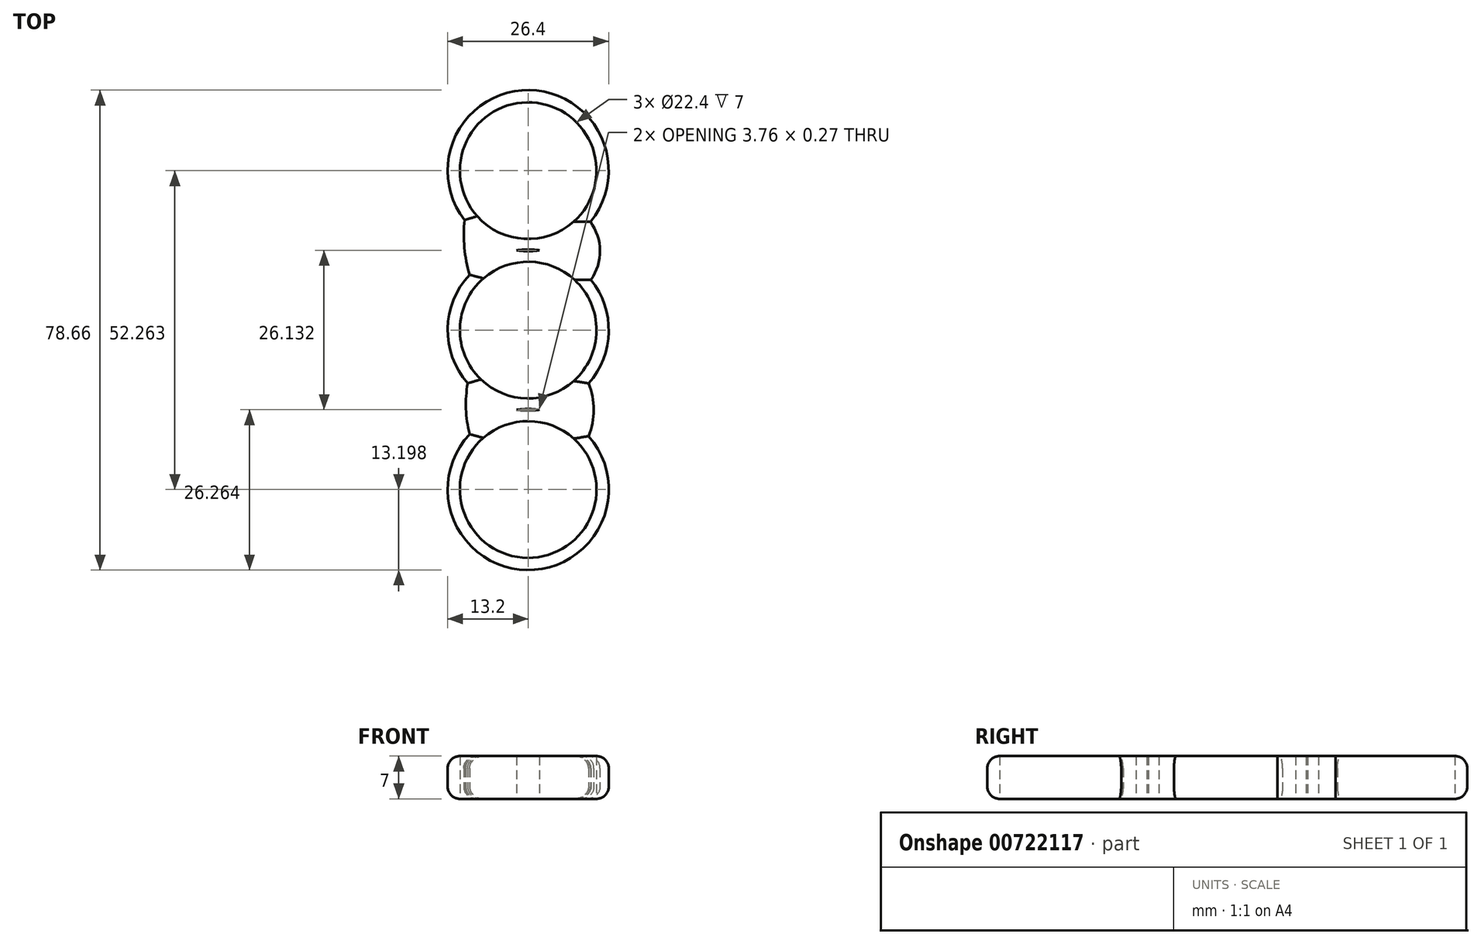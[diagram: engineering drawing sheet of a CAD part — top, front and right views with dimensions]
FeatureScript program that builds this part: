
annotation { "Feature Type Name" : "Feature", "Feature Type Description" : "" }
export const myFeature = defineFeature(function(context is Context, id is Id, definition is map)
    precondition{}
    {
        {
            var Q0;
            Q0=qCreatedBy(makeId("Top.planeOp"),FACE);
            var sketch = newSketch(context, id + "F0", { "sketchPlane" : qUnion([Q0])});
            skCircle(sketch, "E0", {"center": v(0, 0) * mm, "radius": 11.2 * mm});
            skCircle(sketch, "E1", {"center": v(0, 0) * mm, "radius": 13.2 * mm});
            skCircle(sketch, "E2", {"center": v(0, 26.13) * mm, "radius": 11.2 * mm});
            skCircle(sketch, "E3", {"center": v(0, 26.13) * mm, "radius": 13.2 * mm});
            skCircle(sketch, "E4.1.0", {"center": v(0, -26.13) * mm, "radius": 13.2 * mm});
            skCircle(sketch, "E4.1.1", {"center": v(0, -26.13) * mm, "radius": 11.2 * mm});
            skArc(sketch, "E5", {"start": v(10.3, 8.25) * mm, "mid": v(11.77, 13.02) * mm, "end": v(10.2, 17.75) * mm});
            skArc(sketch, "E6", {"start": v(-10.43, 18.04) * mm, "mid": v(-10.45, 13.51) * mm, "end": v(-9.6, 9.06) * mm});
            skArc(sketch, "E7", {"start": v(-9.91, -8.71) * mm, "mid": v(-10.17, -13.38) * mm, "end": v(-9.35, -17.97) * mm});
            skArc(sketch, "E8", {"start": v(9.9, -17.4) * mm, "mid": v(10.76, -13.07) * mm, "end": v(9.9, -8.74) * mm});
            skSolve(sketch);
        }
        {
            var Q0;
            Q0 = qSketchRegion(id + "F0", true);
            extrude(context, id + "F1", {"entities" : qUnion([Q0]), "depth" : 7 * mm, "offsetDistance" : 25 * mm});
        }
        {
            var Q0;
            {var subQ0=sQuery(id+"F0.wireOp",EDGE,"E3");Q0=makeQuery(id+"F1.opExtrude","CAP_EDGE",EDGE,{"disambiguationData":[OSD([subQ0]),TDD([makeQuery(id+"F0.imprint","IMPRINT",EDGE,{"disambiguationData":[TD([[makeQuery(id+"F0.imprint","INTERSECT",VERTEX,{"derivedFrom":[subQ0,sQuery(id+"F0.wireOp",EDGE,"E5")]}),-1.0]])],"derivedFrom":subQ0})])],"isStart":false});}
            var Q1;
            Q1=makeQuery(id+"F1.opExtrude","CAP_EDGE",EDGE,{"disambiguationData":[OSD([sQuery(id+"F0.wireOp",EDGE,"E5")])],"isStart":false});
            var Q2;
            {var subQ0=sQuery(id+"F0.wireOp",EDGE,"E1");Q2=makeQuery(id+"F1.opExtrude","CAP_EDGE",EDGE,{"disambiguationData":[OSD([subQ0]),TDD([makeQuery(id+"F0.imprint","IMPRINT",EDGE,{"disambiguationData":[TD([[makeQuery(id+"F0.imprint","INTERSECT",VERTEX,{"derivedFrom":[subQ0,sQuery(id+"F0.wireOp",EDGE,"E5")]}),1.0]])],"derivedFrom":subQ0})])],"isStart":false});}
            var Q3;
            Q3=makeQuery(id+"F1.opExtrude","CAP_EDGE",EDGE,{"disambiguationData":[OSD([sQuery(id+"F0.wireOp",EDGE,"E8")])],"isStart":false});
            var Q4;
            {var subQ0=sQuery(id+"F0.wireOp",EDGE,"E4.1.0");Q4=makeQuery(id+"F1.opExtrude","CAP_EDGE",EDGE,{"disambiguationData":[OSD([subQ0]),TDD([makeQuery(id+"F0.imprint","IMPRINT",EDGE,{"disambiguationData":[TD([[makeQuery(id+"F0.imprint","INTERSECT",VERTEX,{"derivedFrom":[subQ0,sQuery(id+"F0.wireOp",EDGE,"E8")]}),1.0]])],"derivedFrom":subQ0})])],"isStart":false});}
            var Q5;
            Q5=makeQuery(id+"F1.opExtrude","CAP_EDGE",EDGE,{"disambiguationData":[OSD([sQuery(id+"F0.wireOp",EDGE,"E7")])],"isStart":false});
            var Q6;
            {var subQ0=sQuery(id+"F0.wireOp",EDGE,"E1");Q6=makeQuery(id+"F1.opExtrude","CAP_EDGE",EDGE,{"disambiguationData":[OSD([subQ0]),TDD([makeQuery(id+"F0.imprint","IMPRINT",EDGE,{"disambiguationData":[TD([[makeQuery(id+"F0.imprint","INTERSECT",VERTEX,{"derivedFrom":[subQ0,sQuery(id+"F0.wireOp",EDGE,"E6")]}),-1.0]])],"derivedFrom":subQ0})])],"isStart":false});}
            var Q7;
            Q7=makeQuery(id+"F1.opExtrude","CAP_EDGE",EDGE,{"disambiguationData":[OSD([sQuery(id+"F0.wireOp",EDGE,"E6")])],"isStart":false});
            fillet(context, id + "F2", {"entities" : qUnion([Q0, Q1, Q2, Q3, Q4, Q5, Q6, Q7]), "radius" : 2 * mm, "tangentPropagation" : true, "allowEdgeOverflow" : false});
        }
        {
            var Q0;
            {var subQ0=sQuery(id+"F0.wireOp",EDGE,"E4.1.0");Q0=makeQuery(id+"F1.opExtrude","CAP_EDGE",EDGE,{"disambiguationData":[OSD([subQ0]),TDD([makeQuery(id+"F0.imprint","IMPRINT",EDGE,{"disambiguationData":[TD([[makeQuery(id+"F0.imprint","INTERSECT",VERTEX,{"derivedFrom":[subQ0,sQuery(id+"F0.wireOp",EDGE,"E8")]}),1.0]])],"derivedFrom":subQ0})])],"isStart":true});}
            var Q1;
            Q1=makeQuery(id+"F1.opExtrude","CAP_EDGE",EDGE,{"disambiguationData":[OSD([sQuery(id+"F0.wireOp",EDGE,"E8")])],"isStart":true});
            var Q2;
            {var subQ0=sQuery(id+"F0.wireOp",EDGE,"E1");Q2=makeQuery(id+"F1.opExtrude","CAP_EDGE",EDGE,{"disambiguationData":[OSD([subQ0]),TDD([makeQuery(id+"F0.imprint","IMPRINT",EDGE,{"disambiguationData":[TD([[makeQuery(id+"F0.imprint","INTERSECT",VERTEX,{"derivedFrom":[subQ0,sQuery(id+"F0.wireOp",EDGE,"E5")]}),1.0]])],"derivedFrom":subQ0})])],"isStart":true});}
            var Q3;
            Q3=makeQuery(id+"F1.opExtrude","CAP_EDGE",EDGE,{"disambiguationData":[OSD([sQuery(id+"F0.wireOp",EDGE,"E5")])],"isStart":true});
            var Q4;
            Q4=makeQuery(id+"F1.opExtrude","CAP_EDGE",EDGE,{"disambiguationData":[OSD([sQuery(id+"F0.wireOp",EDGE,"E6")])],"isStart":true});
            var Q5;
            Q5=makeQuery(id+"F1.opExtrude","CAP_EDGE",EDGE,{"disambiguationData":[OSD([sQuery(id+"F0.wireOp",EDGE,"E7")])],"isStart":true});
            var Q6;
            {var subQ0=sQuery(id+"F0.wireOp",EDGE,"E3");Q6=makeQuery(id+"F1.opExtrude","CAP_EDGE",EDGE,{"disambiguationData":[OSD([subQ0]),TDD([makeQuery(id+"F0.imprint","IMPRINT",EDGE,{"disambiguationData":[TD([[makeQuery(id+"F0.imprint","INTERSECT",VERTEX,{"derivedFrom":[subQ0,sQuery(id+"F0.wireOp",EDGE,"E5")]}),-1.0]])],"derivedFrom":subQ0})])],"isStart":true});}
            var Q7;
            {var subQ0=sQuery(id+"F0.wireOp",EDGE,"E1");Q7=makeQuery(id+"F1.opExtrude","CAP_EDGE",EDGE,{"disambiguationData":[OSD([subQ0]),TDD([makeQuery(id+"F0.imprint","IMPRINT",EDGE,{"disambiguationData":[TD([[makeQuery(id+"F0.imprint","INTERSECT",VERTEX,{"derivedFrom":[subQ0,sQuery(id+"F0.wireOp",EDGE,"E6")]}),-1.0]])],"derivedFrom":subQ0})])],"isStart":true});}
            fillet(context, id + "F3", {"entities" : qUnion([Q0, Q1, Q2, Q3, Q4, Q5, Q6, Q7]), "radius" : 2 * mm, "tangentPropagation" : true, "allowEdgeOverflow" : false});
        }
    });
